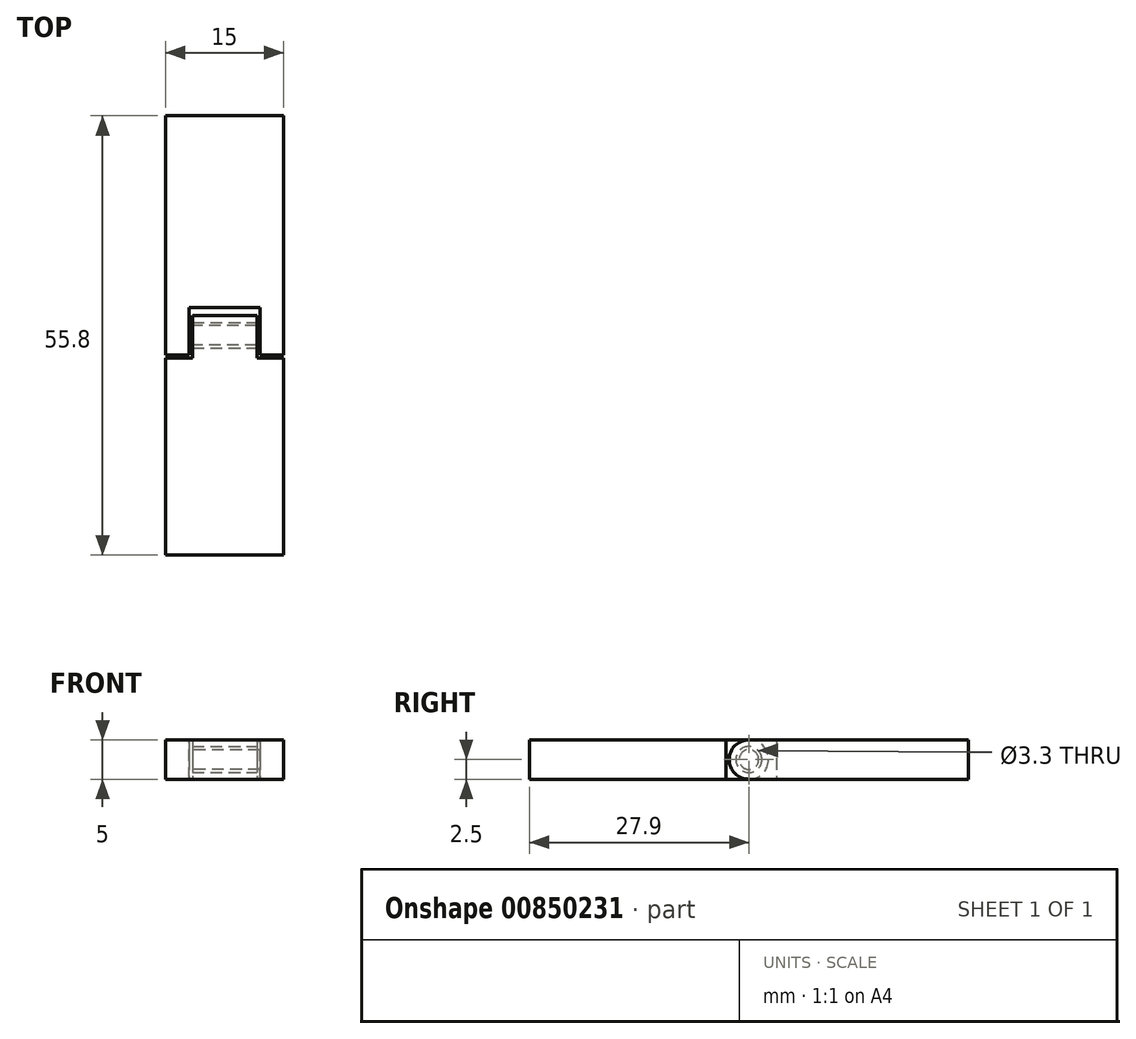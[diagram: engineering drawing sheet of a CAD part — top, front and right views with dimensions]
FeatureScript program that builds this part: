
annotation { "Feature Type Name" : "Feature", "Feature Type Description" : "" }
export const myFeature = defineFeature(function(context is Context, id is Id, definition is map)
    precondition{}
    {
        {
            var Q0;
            Q0=qCreatedBy(makeId("Top.planeOp"),FACE);
            var sketch = newSketch(context, id + "F0", { "sketchPlane" : qUnion([Q0])});
            skLineSegment(sketch, "E0.bottom", {"start": v(-7.5, 0) * mm, "end": v(7.5, 0) * mm});
            skLineSegment(sketch, "E0.top", {"start": v(-7.5, 25) * mm, "end": v(7.5, 25) * mm});
            skLineSegment(sketch, "E0.left", {"start": v(-7.5, 0) * mm, "end": v(-7.5, 25) * mm});
            skLineSegment(sketch, "E0.right", {"start": v(7.5, 0) * mm, "end": v(7.5, 25) * mm});
            skSolve(sketch);
        }
        {
            var Q0;
            Q0=makeQuery(id+"F0.imprint","IMPRINT",FACE,{"disambiguationData":[TD([[makeQuery(id+"F0.imprint","IMPRINT",EDGE,{"derivedFrom":sQuery(id+"F0.wireOp",EDGE,"E0.bottom")}),1.0]])]});
            extrude(context, id + "F1", {"entities" : qUnion([Q0]), "depth" : 5 * mm, "offsetDistance" : 25 * mm});
        }
        {
            var Q0;
            Q0=makeQuery(id+"F1.opExtrude","SWEPT_FACE",FACE,{"disambiguationData":[OSD([sQuery(id+"F0.wireOp",EDGE,"E0.bottom")])]});
            var sketch = newSketch(context, id + "F2", { "sketchPlane" : qUnion([Q0])});
            skLineSegment(sketch, "E1.bottom", {"start": v(-4.5, 5) * mm, "end": v(4.5, 5) * mm});
            skLineSegment(sketch, "E1.top", {"start": v(-4.5, 0) * mm, "end": v(4.5, 0) * mm});
            skLineSegment(sketch, "E1.left", {"start": v(-4.5, 5) * mm, "end": v(-4.5, 0) * mm});
            skLineSegment(sketch, "E1.right", {"start": v(4.5, 5) * mm, "end": v(4.5, 0) * mm});
            skSolve(sketch);
        }
        {
            var Q0;
            Q0=makeQuery(id+"F2.imprint","IMPRINT",FACE,{"disambiguationData":[TD([[makeQuery(id+"F2.imprint","IMPRINT",EDGE,{"derivedFrom":sQuery(id+"F2.wireOp",EDGE,"E1.bottom")}),-1.0]])]});
            extrude(context, id + "F3", {"entities" : qUnion([Q0]), "operationType" : NewBodyOperationType.REMOVE, "oppositeDirection" : true, "depth" : 6 * mm, "offsetDistance" : 25 * mm});
        }
        {
            var Q0;
            Q0=makeQuery(id+"F1.opExtrude","SWEPT_FACE",FACE,{"disambiguationData":[OSD([sQuery(id+"F0.wireOp",EDGE,"E0.left")])]});
            var sketch = newSketch(context, id + "F4", { "sketchPlane" : qUnion([Q0])});
            skCircle(sketch, "E2", {"center": v(-2.5, 2.5) * mm, "radius": 2.5 * mm});
            skPoint(sketch, "E2.first.point", {"position": v(0, 2.5) * mm});
            skPoint(sketch, "E2.second.point", {"position": v(-5, 2.5) * mm});
            skPoint(sketch, "E2.second.point.positionSnap0", {"position": v(0, 2.5) * mm});
            skPoint(sketch, "E2.third.point", {"position": v(-2.13, 4.97) * mm});
            skCircle(sketch, "E3", {"center": v(-2.5, 2.5) * mm, "radius": 1.25 * mm});
            skSolve(sketch);
        }
        {
            var Q0;
            {var subQ0=sQuery(id+"F4.wireOp",EDGE,"E2");var subQ1=sQuery(id+"F0.wireOp",EDGE,"E0.left");var subQ2=makeQuery(id+"F1.opExtrude","CAP_EDGE",EDGE,{"disambiguationData":[OSD([subQ1])],"isStart":false});var subQ3=makeQuery(id+"F4.imprint","INTERSECT",VERTEX,{"derivedFrom":[subQ2,subQ0]});Q0=makeQuery(id+"F4.imprint","IMPRINT",FACE,{"disambiguationData":[TD([[makeQuery(id+"F4.imprint","IMPRINT",EDGE,{"disambiguationData":[TD([[subQ3,1.0]])],"derivedFrom":subQ0}),-1.0]])]});}
            var Q1;
            {var subQ0=sQuery(id+"F4.wireOp",EDGE,"E2");var subQ1=sQuery(id+"F0.wireOp",EDGE,"E0.left");var subQ4=makeQuery(id+"F1.opExtrude","CAP_EDGE",EDGE,{"disambiguationData":[OSD([subQ1])],"isStart":true});var subQ5=makeQuery(id+"F4.imprint","INTERSECT",VERTEX,{"derivedFrom":[subQ4,subQ0]});Q1=makeQuery(id+"F4.imprint","IMPRINT",FACE,{"disambiguationData":[TD([[makeQuery(id+"F4.imprint","IMPRINT",EDGE,{"disambiguationData":[TD([[subQ5,-1.0]])],"derivedFrom":subQ0}),-1.0]])]});}
            var Q2;
            Q2=makeQuery(id+"F1.opExtrude","SWEPT_FACE",FACE,{"disambiguationData":[OSD([sQuery(id+"F0.wireOp",EDGE,"E0.right")])]});
            extrude(context, id + "F5", {"entities" : qUnion([Q0, Q1]), "operationType" : NewBodyOperationType.REMOVE, "endBound" : BoundingType.UP_TO_SURFACE, "oppositeDirection" : true, "depth" : 25 * mm, "endBoundEntityFace" : qUnion([Q2]), "offsetDistance" : 25 * mm});
        }
        {
            var Q0;
            Q0=makeQuery(id+"F4.imprint","IMPRINT",FACE,{"disambiguationData":[TD([[makeQuery(id+"F4.imprint","IMPRINT",EDGE,{"derivedFrom":sQuery(id+"F4.wireOp",EDGE,"E3")}),1.0]])]});
            var Q1;
            Q1=makeQuery(id+"F1.opExtrude","SWEPT_FACE",FACE,{"disambiguationData":[OSD([sQuery(id+"F0.wireOp",EDGE,"E0.right")])]});
            extrude(context, id + "F6", {"entities" : qUnion([Q0]), "operationType" : NewBodyOperationType.ADD, "endBound" : BoundingType.UP_TO_SURFACE, "oppositeDirection" : true, "depth" : 25 * mm, "endBoundEntityFace" : qUnion([Q1]), "offsetDistance" : 25 * mm});
        }
        {
            var Q0;
            Q0=makeQuery(id+"F3.boolean.opBoolean","COPY",FACE,{"derivedFrom":makeQuery(id+"F3.opExtrude","SWEPT_FACE",FACE,{"disambiguationData":[OSD([sQuery(id+"F2.wireOp",EDGE,"E1.right")])]})});
            var sketch = newSketch(context, id + "F7", { "sketchPlane" : qUnion([Q0])});
            skCircle(sketch, "E4", {"center": v(-2.5, 2.5) * mm, "radius": 1.65 * mm});
            skLineSegment(sketch, "E5.bottom", {"start": v(0, 5) * mm, "end": v(-5, 5) * mm});
            skLineSegment(sketch, "E5.top", {"start": v(0, 0) * mm, "end": v(-5, 0) * mm});
            skLineSegment(sketch, "E5.left", {"start": v(0, 5) * mm, "end": v(0, 0) * mm});
            skLineSegment(sketch, "E5.right", {"start": v(-5, 5) * mm, "end": v(-5, 0) * mm});
            skPoint(sketch, "E5.cornerSnap0", {"position": v(0, 2.5) * mm});
            skCircle(sketch, "E6", {"center": v(-2.5, 2.5) * mm, "radius": 2.5 * mm});
            skSolve(sketch);
        }
        {
            var Q0;
            Q0=makeQuery(id+"F7.imprint","IMPRINT",FACE,{"disambiguationData":[TD([[makeQuery(id+"F7.imprint","IMPRINT",EDGE,{"derivedFrom":sQuery(id+"F7.wireOp",EDGE,"E4")}),-1.0]])]});
            var Q1;
            {var subQ0=sQuery(id+"F7.wireOp",EDGE,"E5.bottom");var subQ6=sQuery(id+"F7.wireOp",EDGE,"E5.left");var subQ7=makeQuery(id+"F7.imprint","INTERSECT",VERTEX,{"derivedFrom":[subQ0,subQ6]});Q1=makeQuery(id+"F7.imprint","IMPRINT",FACE,{"disambiguationData":[TD([[makeQuery(id+"F7.imprint","IMPRINT",EDGE,{"disambiguationData":[TD([[subQ7,-1.0]])],"derivedFrom":subQ0}),1.0]])]});}
            var Q2;
            {var subQ0=sQuery(id+"F7.wireOp",EDGE,"E5.top");var subQ6=sQuery(id+"F7.wireOp",EDGE,"E5.left");var subQ7=makeQuery(id+"F7.imprint","INTERSECT",VERTEX,{"derivedFrom":[subQ0,subQ6]});Q2=makeQuery(id+"F7.imprint","IMPRINT",FACE,{"disambiguationData":[TD([[makeQuery(id+"F7.imprint","IMPRINT",EDGE,{"disambiguationData":[TD([[subQ7,-1.0]])],"derivedFrom":subQ0}),-1.0]])]});}
            var Q3;
            Q3=makeQuery(id+"F3.boolean.opBoolean","COPY",FACE,{"derivedFrom":makeQuery(id+"F3.opExtrude","SWEPT_FACE",FACE,{"disambiguationData":[OSD([sQuery(id+"F2.wireOp",EDGE,"E1.left")])]})});
            extrude(context, id + "F8", {"entities" : qUnion([Q0, Q1, Q2]), "endBound" : BoundingType.UP_TO_SURFACE, "depth" : 25 * mm, "endBoundEntityFace" : qUnion([Q3]), "offsetDistance" : 25 * mm});
        }
        {
            var Q0;
            Q0=makeQuery(id+"F8.opExtrude","CAP_FACE",FACE,{"disambiguationData":[OSD([sQuery(id+"F7.wireOp",EDGE,"E4"),sQuery(id+"F7.wireOp",EDGE,"E5.bottom"),sQuery(id+"F7.wireOp",EDGE,"E5.top"),sQuery(id+"F7.wireOp",EDGE,"E5.left"),sQuery(id+"F7.wireOp",EDGE,"E6")])],"isStart":false});
            extrude(context, id + "F9", {"entities" : qUnion([Q0]), "operationType" : NewBodyOperationType.REMOVE, "oppositeDirection" : true, "depth" : .4 * mm, "offsetDistance" : 25 * mm});
        }
        {
            var Q0;
            Q0=makeQuery(id+"F8.opExtrude","CAP_FACE",FACE,{"disambiguationData":[OSD([sQuery(id+"F7.wireOp",EDGE,"E4"),sQuery(id+"F7.wireOp",EDGE,"E5.bottom"),sQuery(id+"F7.wireOp",EDGE,"E5.top"),sQuery(id+"F7.wireOp",EDGE,"E5.left"),sQuery(id+"F7.wireOp",EDGE,"E6")])],"isStart":true});
            extrude(context, id + "F10", {"entities" : qUnion([Q0]), "operationType" : NewBodyOperationType.REMOVE, "oppositeDirection" : true, "depth" : .4 * mm, "offsetDistance" : 25 * mm});
        }
        {
            var Q0;
            Q0=makeQuery(id+"F8.opExtrude","SWEPT_FACE",FACE,{"disambiguationData":[OSD([sQuery(id+"F7.wireOp",EDGE,"E5.left")])]});
            extrude(context, id + "F11", {"entities" : qUnion([Q0]), "operationType" : NewBodyOperationType.ADD, "depth" : .4 * mm, "offsetDistance" : 25 * mm});
        }
        {
            var Q0;
            Q0=makeQuery(id+"F11.opExtrude","CAP_FACE",FACE,{"disambiguationData":[OSD([sQuery(id+"F7.wireOp",EDGE,"E5.left")])],"isStart":false});
            var sketch = newSketch(context, id + "F12", { "sketchPlane" : qUnion([Q0])});
            skPoint(sketch, "E7.0", {"position": v(-7.5, 5) * mm});
            skPoint(sketch, "E8.0", {"position": v(7.5, 0) * mm});
            skLineSegment(sketch, "E9.bottom", {"start": v(-7.5, 5) * mm, "end": v(7.5, 5) * mm});
            skLineSegment(sketch, "E9.top", {"start": v(-7.5, 0) * mm, "end": v(7.5, 0) * mm});
            skLineSegment(sketch, "E9.left", {"start": v(-7.5, 5) * mm, "end": v(-7.5, 0) * mm});
            skLineSegment(sketch, "E9.right", {"start": v(7.5, 5) * mm, "end": v(7.5, 0) * mm});
            skSolve(sketch);
        }
        {
            var Q0;
            Q0 = qSketchRegion(id + "F12", true);
            extrude(context, id + "F13", {"entities" : qUnion([Q0]), "operationType" : NewBodyOperationType.ADD, "depth" : 25 * mm, "offsetDistance" : 25 * mm});
        }
        {
            var Q0;
            Q0=makeQuery(id+"F1.opExtrude","SWEPT_FACE",FACE,{"disambiguationData":[OSD([sQuery(id+"F0.wireOp",EDGE,"E0.top")])]});
            extrude(context, id + "F14", {"entities" : qUnion([Q0]), "operationType" : NewBodyOperationType.ADD, "depth" : 5.4 * mm, "offsetDistance" : 25 * mm});
        }
    });
